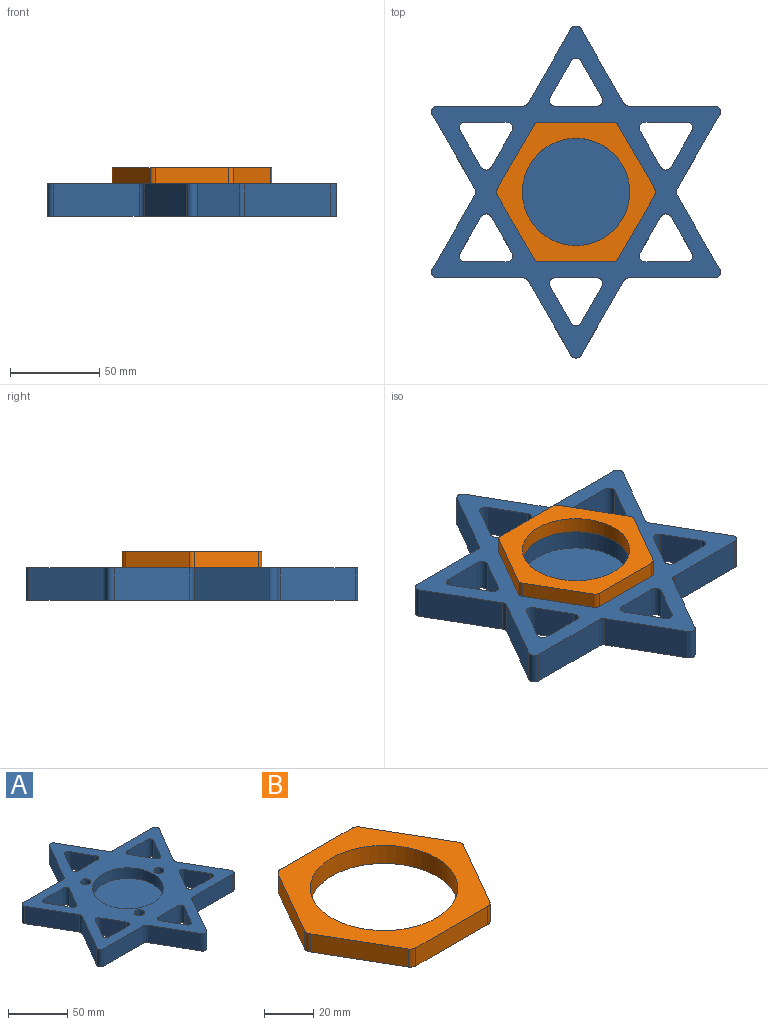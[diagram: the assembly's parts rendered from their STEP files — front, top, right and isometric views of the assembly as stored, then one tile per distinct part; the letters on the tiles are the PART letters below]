
ASSEMBLY  parts=2 mates=1
PART A: 67 faces, bbox 161.5x185.5x18 mm
  f0: cylinder r=3.25mm len=18mm, axis (0,0,-1), area 122.5mm2, adj f1,f53,f54,f55
  f1: plane 20.25x18mm, normal (-0.87,-0.5,0), area 420.9mm2, adj f0,f2,f54,f55
  f2: cylinder r=3.25mm len=18mm, axis (0,0,-1), area 122.5mm2, adj f1,f3,f54,f55
  f3: plane 23.38x18mm, normal (0,1,0), area 420.9mm2, adj f2,f4,f54,f55
  f4: cylinder r=3.25mm len=18mm, axis (0,0,-1), area 122.5mm2, adj f3,f53,f54,f55
  f5: cylinder r=3.25mm len=18mm, axis (0,0,-1), area 61.3mm2, adj f6,f47,f54,f55
  f6: plane 41.5x23.96mm, normal (0.87,0.5,0), area 862.6mm2, adj f5,f54,f55,f61
  f7: plane 41.5x23.96mm, normal (-0.87,0.5,0), area 862.6mm2, adj f8,f54,f55,f61
  f8: cylinder r=3.25mm len=18mm, axis (0,0,-1), area 61.3mm2, adj f7,f9,f54,f55
  f9: plane 47.92x18mm, normal (0,1,0), area 862.6mm2, adj f8,f54,f55,f62
  f10: plane 41.5x23.96mm, normal (-0.87,-0.5,0), area 862.6mm2, adj f11,f54,f55,f62
  f11: cylinder r=3.25mm len=18mm, axis (0,0,-1), area 61.3mm2, adj f10,f12,f54,f55
  f12: plane 41.5x23.96mm, normal (-0.87,0.5,0), area 862.6mm2, adj f11,f54,f55,f63
  f13: plane 47.92x18mm, normal (0,-1,0), area 862.6mm2, adj f14,f54,f55,f63
  f14: cylinder r=3.25mm len=18mm, axis (0,0,-1), area 61.3mm2, adj f13,f15,f54,f55
  f15: plane 41.5x23.96mm, normal (-0.87,-0.5,0), area 862.6mm2, adj f14,f54,f55,f64
  f16: plane 41.5x23.96mm, normal (0.87,-0.5,0), area 862.6mm2, adj f17,f54,f55,f64
  f17: cylinder r=3.25mm len=18mm, axis (0,0,-1), area 61.3mm2, adj f16,f18,f54,f55
  f18: plane 47.92x18mm, normal (0,-1,0), area 862.6mm2, adj f17,f54,f55,f65
  f19: plane 41.5x23.96mm, normal (0.87,0.5,0), area 862.6mm2, adj f20,f54,f55,f65
  f20: cylinder r=3.25mm len=18mm, axis (0,0,-1), area 61.3mm2, adj f19,f21,f54,f55
  f21: plane 41.5x23.96mm, normal (0.87,-0.5,0), area 862.6mm2, adj f20,f54,f55,f66
  f22: plane 20.25x18mm, normal (0.87,-0.5,0), area 420.9mm2, adj f23,f48,f54,f55
  f23: cylinder r=3.25mm len=18mm, axis (0,0,-1), area 122.5mm2, adj f22,f24,f54,f55
  f24: plane 20.25x18mm, normal (-0.87,-0.5,0), area 420.9mm2, adj f23,f25,f54,f55
  f25: cylinder r=3.25mm len=18mm, axis (0,0,-1), area 122.5mm2, adj f24,f26,f54,f55
  f26: plane 23.38x18mm, normal (0,1,0), area 420.9mm2, adj f25,f48,f54,f55
  f27: plane 20.25x18mm, normal (0.87,0.5,0), area 420.9mm2, adj f28,f49,f54,f55
  f28: cylinder r=3.25mm len=18mm, axis (0,0,-1), area 122.5mm2, adj f27,f29,f54,f55
  f29: plane 23.38x18mm, normal (0,-1,0), area 420.9mm2, adj f28,f30,f54,f55
  f30: cylinder r=3.25mm len=18mm, axis (0,0,-1), area 122.5mm2, adj f29,f31,f54,f55
  f31: plane 20.25x18mm, normal (-0.87,0.5,0), area 420.9mm2, adj f30,f49,f54,f55
  f32: plane 20.25x18mm, normal (-0.87,0.5,0), area 420.9mm2, adj f33,f50,f54,f55
  f33: cylinder r=3.25mm len=18mm, axis (0,0,-1), area 122.5mm2, adj f32,f34,f54,f55
  f34: plane 20.25x18mm, normal (0.87,0.5,0), area 420.9mm2, adj f33,f35,f54,f55
  f35: cylinder r=3.25mm len=18mm, axis (0,0,-1), area 122.5mm2, adj f34,f36,f54,f55
  f36: plane 23.38x18mm, normal (0,-1,0), area 420.9mm2, adj f35,f50,f54,f55
  f37: plane 20.25x18mm, normal (-0.87,-0.5,0), area 420.9mm2, adj f38,f51,f54,f55
  f38: cylinder r=3.25mm len=18mm, axis (0,0,-1), area 122.5mm2, adj f37,f39,f54,f55
  f39: plane 23.38x18mm, normal (0,1,0), area 420.9mm2, adj f38,f40,f54,f55
  f40: cylinder r=3.25mm len=18mm, axis (0,0,-1), area 122.5mm2, adj f39,f41,f54,f55
  f41: plane 20.25x18mm, normal (0.87,-0.5,0), area 420.9mm2, adj f40,f51,f54,f55
  f42: plane 23.38x18mm, normal (0,-1,0), area 420.9mm2, adj f43,f52,f54,f55
  f43: cylinder r=3.25mm len=18mm, axis (0,0,-1), area 122.5mm2, adj f42,f44,f54,f55
  f44: plane 20.25x18mm, normal (-0.87,0.5,0), area 420.9mm2, adj f43,f45,f54,f55
  f45: cylinder r=3.25mm len=18mm, axis (0,0,-1), area 122.5mm2, adj f44,f46,f54,f55
  f46: plane 20.25x18mm, normal (0.87,0.5,0), area 420.9mm2, adj f45,f52,f54,f55
  f47: plane 47.92x18mm, normal (0,1,0), area 862.6mm2, adj f5,f54,f55,f66
  f48: cylinder r=3.25mm len=18mm, axis (0,0,-1), area 122.5mm2, adj f22,f26,f54,f55
  f49: cylinder r=3.25mm len=18mm, axis (0,0,-1), area 122.5mm2, adj f27,f31,f54,f55
  f50: cylinder r=3.25mm len=18mm, axis (0,0,-1), area 122.5mm2, adj f32,f36,f54,f55
  f51: cylinder r=3.25mm len=18mm, axis (0,0,-1), area 122.5mm2, adj f37,f41,f54,f55
  f52: cylinder r=3.25mm len=18mm, axis (0,0,-1), area 122.5mm2, adj f42,f46,f54,f55
  f53: plane 20.25x18mm, normal (0.87,-0.5,0), area 420.9mm2, adj f0,f4,f54,f55
  f54: plane 185.5x161.52mm, normal (0,0,1), area 9941.4mm2, adj f0,f1,f2,f3,f4,f5,f6,f7
  f55: plane 185.5x161.52mm, normal (0,0,-1), area 12768.8mm2, adj f0,f1,f2,f3,f4,f5,f6,f7
  f56: cylinder r=30mm len=60mm, axis (0,0,1), area 2073.5mm2, adj f54,f57
  f57: plane 60x60mm, normal (0,0,1), area 2827.4mm2, adj f56
  f58: cylinder r=4.2mm len=18mm, axis (0,0,1), area 475mm2, adj f54,f55
  f59: cylinder r=4.2mm len=18mm, axis (0,0,1), area 475mm2, adj f54,f55
  f60: cylinder r=4.2mm len=18mm, axis (0,0,1), area 475mm2, adj f54,f55
  f61: cylinder r=3.25mm len=18mm, axis (0,0,-1), area 122.5mm2, adj f6,f7,f54,f55
  f62: cylinder r=3.25mm len=18mm, axis (0,0,-1), area 122.5mm2, adj f9,f10,f54,f55
  f63: cylinder r=3.25mm len=18mm, axis (0,0,-1), area 122.5mm2, adj f12,f13,f54,f55
  f64: cylinder r=3.25mm len=18mm, axis (0,0,-1), area 122.5mm2, adj f15,f16,f54,f55
  f65: cylinder r=3.25mm len=18mm, axis (0,0,-1), area 122.5mm2, adj f18,f19,f54,f55
  f66: cylinder r=3.25mm len=18mm, axis (0,0,-1), area 122.5mm2, adj f21,f47,f54,f55
PART B: 21 faces, bbox 89.1x78x9 mm
  f0: cylinder r=4.2mm len=8.4mm, axis (0,0,-1), area 118.8mm2, adj f11,f14
  f1: cylinder r=4.2mm len=8.4mm, axis (0,0,-1), area 118.8mm2, adj f11,f13
  f2: cylinder r=4.2mm len=8.4mm, axis (0,0,-1), area 118.8mm2, adj f11,f12
  f3: plane 41.28x9mm, normal (0,-1,0), area 371.5mm2, adj f10,f11,f15,f20
  f4: plane 35.75x20.64mm, normal (0.87,-0.5,0), area 371.5mm2, adj f10,f11,f15,f16
  f5: plane 35.75x20.64mm, normal (0.87,0.5,0), area 371.5mm2, adj f10,f11,f16,f17
  f6: plane 41.28x9mm, normal (0,1,0), area 371.5mm2, adj f10,f11,f17,f18
  f7: plane 35.75x20.64mm, normal (-0.87,0.5,0), area 371.5mm2, adj f10,f11,f18,f19
  f8: cylinder r=30mm len=60mm, axis (0,0,-1), area 1696.5mm2, adj f10,f11
  f9: plane 35.75x20.64mm, normal (-0.87,-0.5,0), area 371.5mm2, adj f10,f11,f19,f20
  f10: plane 89.06x78mm, normal (0,0,1), area 2438.1mm2, adj f3,f4,f5,f6,f7,f8,f9,f15
  f11: plane 89.06x78mm, normal (0,0,-1), area 2271.8mm2, adj f0,f1,f2,f3,f4,f5,f6,f7
  f12: plane 8.4x8.4mm, normal (0,0,-1), area 55.4mm2, adj f2
  f13: plane 8.4x8.4mm, normal (0,0,-1), area 55.4mm2, adj f1
  f14: plane 8.4x8.4mm, normal (0,0,-1), area 55.4mm2, adj f0
  f15: cylinder r=3.25mm len=9mm, axis (0,0,-1), area 30.6mm2, adj f3,f4,f10,f11
  f16: cylinder r=3.25mm len=9mm, axis (0,0,-1), area 30.6mm2, adj f4,f5,f10,f11
  f17: cylinder r=3.25mm len=9mm, axis (0,0,-1), area 30.6mm2, adj f5,f6,f10,f11
  f18: cylinder r=3.25mm len=9mm, axis (0,0,-1), area 30.6mm2, adj f6,f7,f10,f11
  f19: cylinder r=3.25mm len=9mm, axis (0,0,-1), area 30.6mm2, adj f7,f9,f10,f11
  f20: cylinder r=3.25mm len=9mm, axis (0,0,-1), area 30.6mm2, adj f3,f9,f10,f11
PLACE A at identity fixed
PLACE B t=(0,0,18)mm
MATE fastened A.f56 <-> B.f8  axis (0,0,1) through (0,0,18)mm
